# Revit family: КП-1
name_source: partatom
category: Арматура воздуховодов
units: mm (PartAtom-declared; Revit-internal decimal feet)

## family parameters
Всегда вертикально = Да
На основе рабочей плоскости = Нет
Общий = Нет
При загрузке вырезать с полостями = Нет
Размер круглого соединителя = Использовать диаметр
Тип детали = Присоединяется

## types (21) — shared parameters
00_20_Manufacturer = Вентс
00_20_Name = Клапан протипожежний вогнезатримувальний
Casing Material = Металл, окрашенный, белый, матовый RAL 5007
Grid Material = Cover Grid Cross
Load Classification = HVAC
Maintenance zone material = <По категории>
Voltage = 230 В
Два фланца = Да
Размещение привода (внутри) = Нет
Размещение привода (снаружи) = Да
zero-valued in all types: Отметка по умолчанию

## per-type parameters (varying)
| type | A | A1 | A2 | A3 | An | B | B1 | B2 | B3 | Bn | Power | Вес |
| КП-1-200х200-2-ПВП230Т-СН | 200 мм | 220 мм | 240 мм | 100 мм | 210 мм | 200 мм | 220 мм | 240 мм | 110 мм | 210 мм | 7 В·А | 6.2 кг |
| КП-1-1000х1000-2-ПВП230Т-СН | 1000 мм | 1030 мм | 1060 мм | 500 мм | 1010 мм | 1000 мм | 1030 мм | 1060 мм | 515 мм | 1010 мм | 11 В·А | 41.7 кг |
| КП-1-250х200-2-ПВП230Т-СН | 250 мм | 270 мм | 290 мм | 125 мм | 260 мм | 200 мм | 220 мм | 240 мм | 110 мм | 210 мм | 10 В·А | 6.8 кг |
| КП-1-250х250-2-ПВП230Т-СН | 250 мм | 270 мм | 290 мм | 125 мм | 260 мм | 250 мм | 270 мм | 290 мм | 135 мм | 260 мм | 10 В·А | 7.3 кг |
| КП-1-300х200-2-ПВП230Т-СН | 300 мм | 320 мм | 340 мм | 150 мм | 310 мм | 200 мм | 220 мм | 240 мм | 110 мм | 210 мм | 10 В·А | 7.3 кг |
| КП-1-300х250-2-ПВП230Т-СН | 300 мм | 320 мм | 340 мм | 150 мм | 310 мм | 250 мм | 270 мм | 290 мм | 135 мм | 260 мм | 10 В·А | 7.9 кг |
| КП-1-300х300-2-ПВП230Т-СН | 300 мм | 320 мм | 340 мм | 150 мм | 310 мм | 300 мм | 320 мм | 340 мм | 160 мм | 310 мм | 10 В·А | 8.5 кг |
| КП-1-400х250-2-ПВП230Т-СН | 400 мм | 420 мм | 440 мм | 200 мм | 410 мм | 250 мм | 270 мм | 290 мм | 135 мм | 260 мм | 10 В·А | 9.1 кг |
| КП-1-400х300-2-ПВП230Т-СН | 400 мм | 420 мм | 440 мм | 200 мм | 410 мм | 300 мм | 320 мм | 340 мм | 160 мм | 310 мм | 10 В·А | 9.8 кг |
| КП-1-400х400-2-ПВП230Т-СН | 400 мм | 420 мм | 440 мм | 200 мм | 410 мм | 400 мм | 420 мм | 440 мм | 210 мм | 410 мм | 10 В·А | 11.3 кг |
| КП-1-500х300-2-ПВП230Т-СН | 500 мм | 520 мм | 540 мм | 250 мм | 510 мм | 300 мм | 320 мм | 340 мм | 160 мм | 310 мм | 10 В·А | 10.7 кг |
| КП-1-500х400-2-ПВП230Т-СН | 500 мм | 520 мм | 540 мм | 250 мм | 510 мм | 400 мм | 420 мм | 440 мм | 210 мм | 410 мм | 10 В·А | 12.9 кг |
| КП-1-500х500-2-ПВП230Т-СН | 500 мм | 530 мм | 560 мм | 250 мм | 510 мм | 500 мм | 530 мм | 560 мм | 265 мм | 510 мм | 10 В·А | 16.6 кг |
| КП-1-600х400-2-ПВП230Т-СН | 600 мм | 620 мм | 640 мм | 300 мм | 610 мм | 400 мм | 420 мм | 440 мм | 210 мм | 410 мм | 10 В·А | 14.5 кг |
| КП-1-600х500-2-ПВП230Т-СН | 600 мм | 630 мм | 660 мм | 300 мм | 610 мм | 500 мм | 530 мм | 560 мм | 265 мм | 510 мм | 11 В·А | 18.4 кг |
| КП-1-600х600-2-ПВП230Т-СН | 600 мм | 630 мм | 660 мм | 300 мм | 610 мм | 600 мм | 630 мм | 660 мм | 315 мм | 610 мм | 11 В·А | 20.6 кг |
| КП-1-800х500-2-ПВП230Т-СН | 800 мм | 830 мм | 860 мм | 400 мм | 810 мм | 500 мм | 530 мм | 560 мм | 265 мм | 510 мм | 11 В·А | 22.3 кг |
| КП-1-800х600-2-ПВП230Т-СН | 800 мм | 830 мм | 860 мм | 400 мм | 810 мм | 600 мм | 630 мм | 660 мм | 315 мм | 610 мм | 11 В·А | 24.8 кг |
| КП-1-800х800-2-ПВП230Т-СН | 800 мм | 830 мм | 860 мм | 400 мм | 810 мм | 800 мм | 830 мм | 860 мм | 415 мм | 810 мм | 11 В·А | 30.1 кг |
| КП-1-1000х600-2-ПВП230Т-СН | 1000 мм | 1030 мм | 1060 мм | 500 мм | 1010 мм | 600 мм | 630 мм | 660 мм | 315 мм | 610 мм | 11 В·А | 29 кг |
| КП-1-1000х800-2-ПВП230Т-СН | 1000 мм | 1030 мм | 1060 мм | 500 мм | 1010 мм | 800 мм | 830 мм | 860 мм | 415 мм | 810 мм | 11 В·А | 35.4 кг |

note: column(s) folded — value = type name in every type: 00_20_Type
